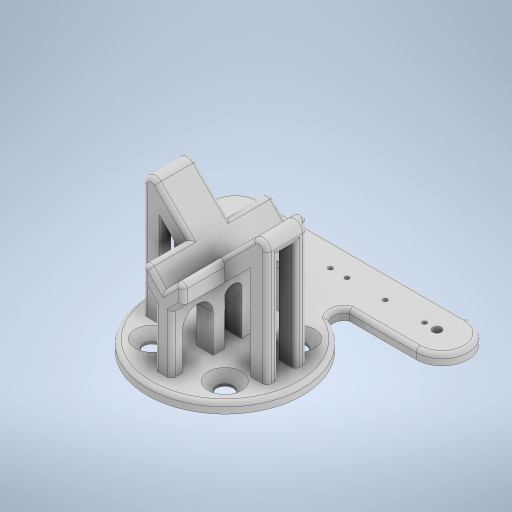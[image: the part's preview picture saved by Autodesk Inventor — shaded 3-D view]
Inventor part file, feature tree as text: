
AUTODESK INVENTOR PART (.ipt)
format: ipt  version: 2024.1 (Build 281209000, 209)  size: 577,024 bytes
history: native  units: in
note: dims shown in document units (in); Inventor stores cm internally (conversion verified against a paired STEP export)
features: sketch x8, extrude x5, fillet x4, hole x3
ambient origin geometry x8: Origin, YZ Plane, XZ Plane, XY Plane, X Axis, Y Axis, Z Axis, Center Point
bodies: Body1 (feature_tree)
feature tree (20):
  extrude  "Extrusion2"  Depth=4.9213in
  extrude  "Extrusion3"  Depth=0.1575in
  extrude  "Extrusion4"  Depth=0.0787in
  extrude  "Extrusion5"  Depth=0.0787in
  fillet  "Fillet1"  Radius=0.8858in
  fillet  "Fillet3"  Radius=1.8701in
  fillet  "Fillet4"  Radius=1.6339in
  hole  "Hole2"  [1 undecoded]
  hole  "Hole3"  [1 undecoded]
  hole  "Hole4"  [1 undecoded]
  extrude  "Extrusion6"  Depth=0.0787in TaperAngle=0.0deg
  fillet  "Fillet5"  [1 undecoded]
  sketch  "Sketch1"  dims[d13=2.9528in d14=4.9213in]
  sketch  "Sketch2"  dims[d15=0.9843in d17=0.1575in]
  sketch  "Sketch3"  dims[d18=0.0787in d19=0.0787in]
  sketch  "Sketch4"  dims[d20=0.0787in d21=0.1575in d22=0.8858in d23=1.8701in d24=1.6339in]
  sketch  "Sketch6"  dims[d27=0.3937in d28=0.3937in]
  sketch  "Sketch7"  dims[d33=0.1969in d34=0.0in d36=0.1969in]
  sketch  "Sketch8"  dims[d37=1.1811in d38=0.1969in]
  sketch  "Sketch9"  dims[d39=1.1811in d40=2.5591in d41=0.0in d43=90.0deg d45=0.315in d46=0.9843in d47=0.0in d48=0.2165in d49=0.2165in d50=2.1654in d51=0.0in d52=0.1575in d54=0.4921in d55=0.0787in d58=2.1654in d66=0.315in d67=0.2362in d68=0.6299in d69=0.0787in d70=90.0deg d71=0.1969in d72=0.8108in d73=0.315in d74=0.2362in d75=0.6299in d76=0.0787in d77=90.0deg d78=0.1969in d79=0.8108in d80=0.315in d81=0.2362in d82=0.6299in d83=0.0787in d84=90.0deg d85=0.1969in d86=0.8108in d87=0.315in d88=0.315in d89=0.315in d90=0.315in d91=0.1969in d92=0.1969in d93=1.1811in d94=1.1811in d95=1.5748in d96=0.0in d97=0.2165in d98=0.2165in d99=0.9843in d100=0.0in d101=0.315in d102=0.0787in d103=0.315in d56=0.0197in d57=0.0344in d59=0.0344in]
note: 4 required parameter values undecoded (feature->parameter linkage not recoverable at this tier; creation-order binding heuristic only, values carry confidence <= 0.55)
